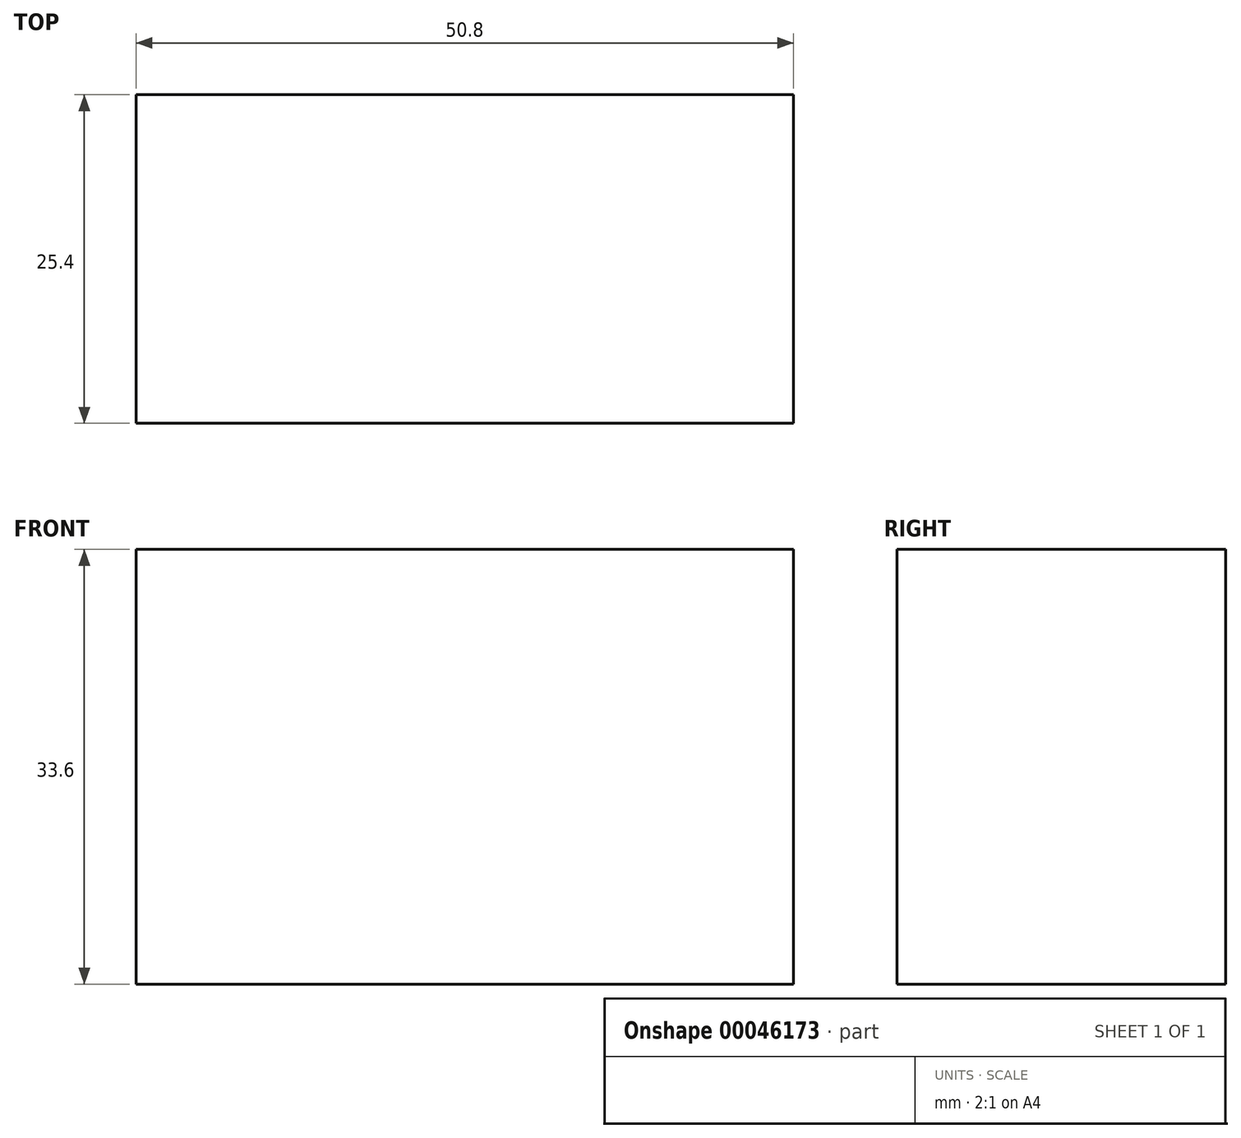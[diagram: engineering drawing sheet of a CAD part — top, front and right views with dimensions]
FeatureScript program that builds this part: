
annotation { "Feature Type Name" : "Feature", "Feature Type Description" : "" }
export const myFeature = defineFeature(function(context is Context, id is Id, definition is map)
    precondition{}
    {
        {
            var Q0;
            Q0=qCreatedBy(makeId("Top.planeOp"),FACE);
            var sketch = newSketch(context, id + "F0", { "sketchPlane" : qUnion([Q0])});
            skLineSegment(sketch, "E0.bottom", {"start": v(0, 0) * mm, "end": v(-50.8, 0) * mm});
            skLineSegment(sketch, "E0.top", {"start": v(0, 25.4) * mm, "end": v(-50.8, 25.4) * mm});
            skLineSegment(sketch, "E0.left", {"start": v(0, 0) * mm, "end": v(0, 25.4) * mm});
            skLineSegment(sketch, "E0.right", {"start": v(-50.8, 0) * mm, "end": v(-50.8, 25.4) * mm});
            skSolve(sketch);
        }
        {
            var Q0;
            Q0=makeQuery(id+"F0.imprint","IMPRINT",FACE,{"disambiguationData":[TD([[makeQuery(id+"F0.imprint","IMPRINT",EDGE,{"derivedFrom":sQuery(id+"F0.wireOp",EDGE,"E0.bottom")}),-1.0]])]});
            extrude(context, id + "F1", {"entities" : qUnion([Q0]), "depth" : 33.6 * mm});
        }
    });
